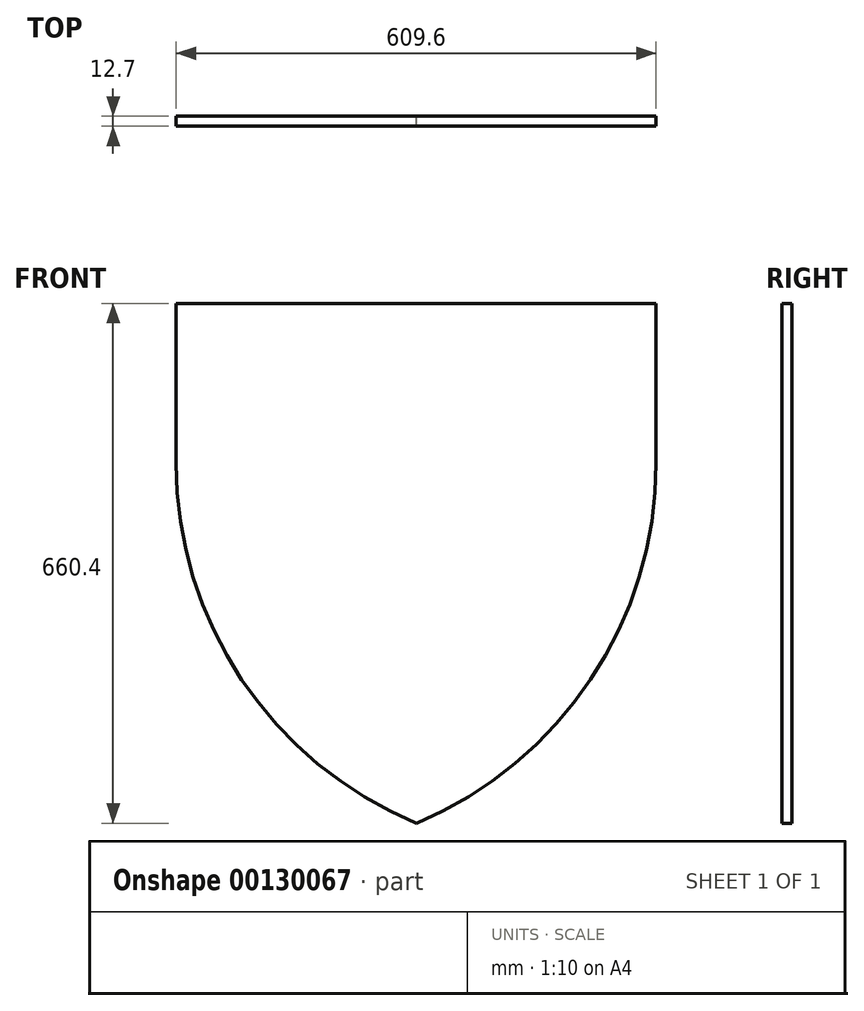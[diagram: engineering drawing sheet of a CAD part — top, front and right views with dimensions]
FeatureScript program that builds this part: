
annotation { "Feature Type Name" : "Feature", "Feature Type Description" : "" }
export const myFeature = defineFeature(function(context is Context, id is Id, definition is map)
    precondition{}
    {
        {
            var Q0;
            Q0=qCreatedBy(makeId("Front.planeOp"),FACE);
            var sketch = newSketch(context, id + "F0", { "sketchPlane" : qUnion([Q0])});
            skLineSegment(sketch, "E0", {"start": v(-305.32, 695) * mm, "end": v(304.28, 695) * mm});
            skLineSegment(sketch, "E1", {"start": v(-305.32, 695) * mm, "end": v(-305.32, 491.8) * mm});
            skLineSegment(sketch, "E2", {"start": v(304.28, 695) * mm, "end": v(304.28, 491.8) * mm});
            skArc(sketch, "E3", {"start": v(-305.32, 491.8) * mm, "mid": v(-221.97, 216.9) * mm, "end": v(0, 34.6) * mm});
            skArc(sketch, "E4", {"start": v(0, 34.6) * mm, "mid": v(221.26, 217.2) * mm, "end": v(304.28, 491.8) * mm});
            skSolve(sketch);
        }
        {
            var Q0;
            Q0 = qSketchRegion(id + "F0", true);
            extrude(context, id + "F1", {"entities" : qUnion([Q0]), "depth" : 12.7 * mm});
        }
    });
